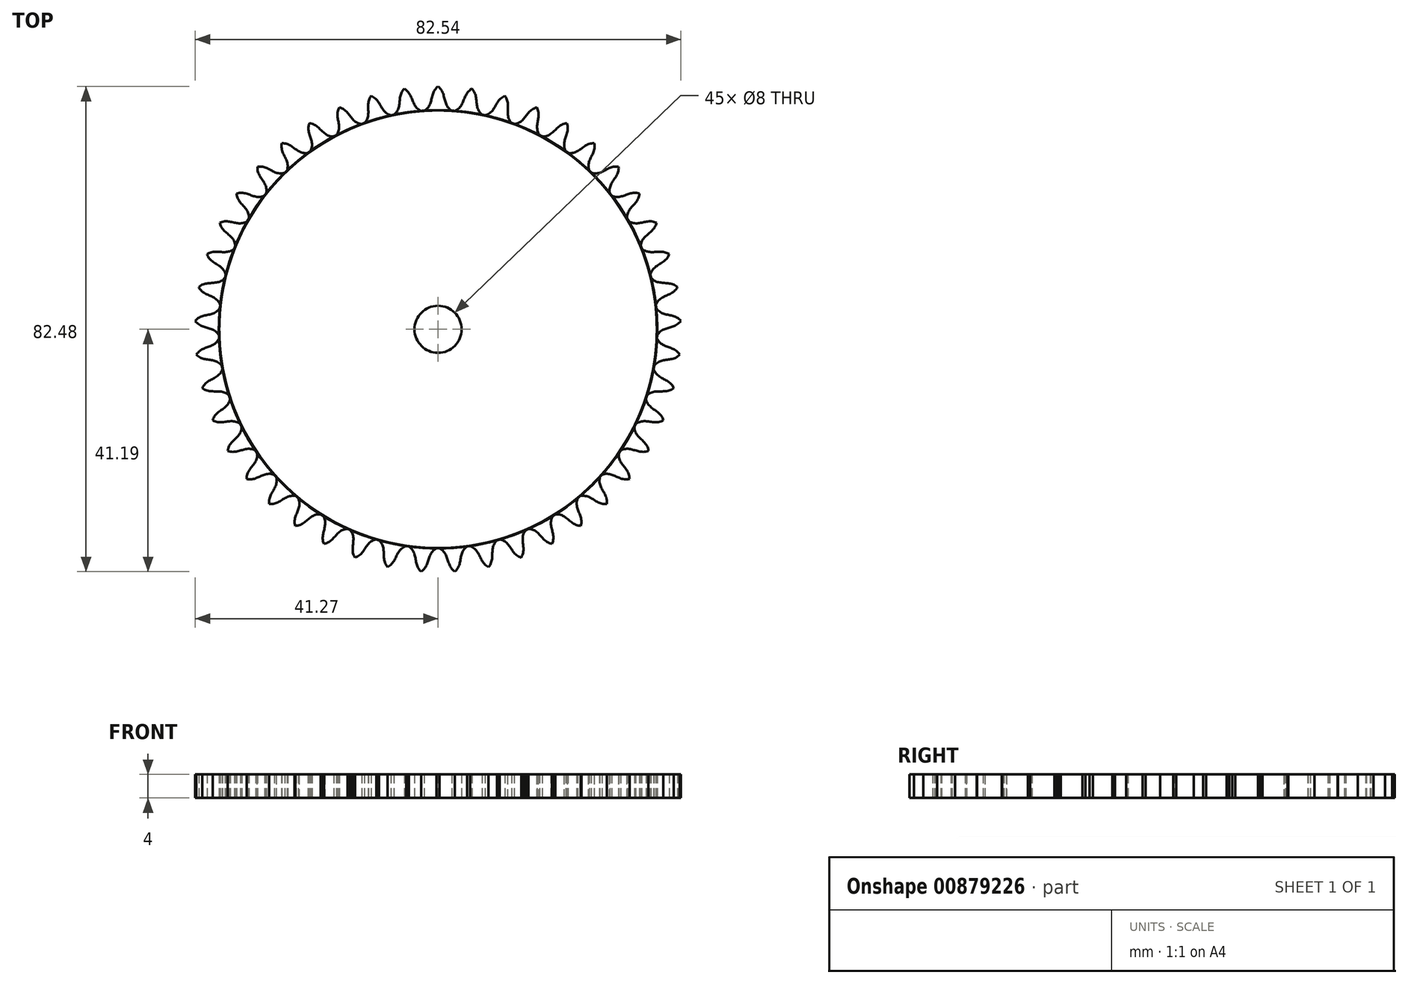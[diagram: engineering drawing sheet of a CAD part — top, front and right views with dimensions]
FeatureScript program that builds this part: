
annotation { "Feature Type Name" : "Feature", "Feature Type Description" : "" }
export const myFeature = defineFeature(function(context is Context, id is Id, definition is map)
    precondition{}
    {
        {
            assignVariable(context, id + "F0", {"name" : "GearWidth", "anyValue" : 4});
        }
        {
            assignVariable(context, id + "F1", {"name" : "TeethNumber", "anyValue" : 45});
        }
        {
            var Q0;
            Q0=qCreatedBy(makeId("Top.planeOp"),FACE);
            var sketch = newSketch(context, id + "F2", { "sketchPlane" : qUnion([Q0])});
            skLineSegment(sketch, "E0", {"start": v(0, 16.9) * mm, "end": v(0, -4.28) * mm, "construction": true});
            skCircle(sketch, "E1", {"center": v(0, 0) * mm, "radius": 37.24 * mm});
            skCircle(sketch, "E2", {"center": v(0, 0) * mm, "radius": 6 * mm});
            skCircle(sketch, "E3", {"center": v(0, 0) * mm, "radius": 4 * mm});
            skPoint(sketch, "E4", {"position": v(0, -6) * mm});
            skPoint(sketch, "E5", {"position": v(0, -5.14) * mm});
            skFitSpline(sketch, "E6", {"points": [v(0, 41.3) * mm, v(-2.35, 37.17) * mm], "startDerivative": vector(-4.5, -3.38) * mm, "endDerivative": vector(-5.1, -3) * mm});
            skFitSpline(sketch, "E7.MirrorCS", {"points": [v(0, 41.3) * mm, v(2.35, 37.17) * mm], "startDerivative": vector(4.5, -3.38) * mm, "endDerivative": vector(5.1, -3) * mm});
            skSolve(sketch);
        }
        {
            var Q0;
            Q0=makeQuery(id+"F2.imprint","IMPRINT",FACE,{"disambiguationData":[TD([[makeQuery(id+"F2.imprint","IMPRINT",EDGE,{"derivedFrom":sQuery(id+"F2.wireOp",EDGE,"E2")}),-1.0]])]});
            var Q1;
            Q1=makeQuery(id+"F2.imprint","IMPRINT",FACE,{"disambiguationData":[TD([[makeQuery(id+"F2.imprint","IMPRINT",EDGE,{"derivedFrom":sQuery(id+"F2.wireOp",EDGE,"E2")}),1.0]])]});
            var Q2;
            {var subQ0=sQuery(id+"F2.wireOp",EDGE,"E6");Q2=makeQuery(id+"F2.imprint","IMPRINT",FACE,{"disambiguationData":[TD([[makeQuery(id+"F2.imprint","IMPRINT",EDGE,{"derivedFrom":subQ0}),1.0]])]});}
            extrude(context, id + "F3", {"entities" : qUnion([Q0, Q1, Q2]), "depth" : (getVariable(context, 'GearWidth')) * mm, "offsetDistance" : 25 * mm});
        }
        {
            var Q0;
            Q0=makeQuery(id+"F3.opExtrude","SWEPT_BODY",BODY,{"disambiguationData":[OSD([sQuery(id+"F2.wireOp",EDGE,"f96d612a-3d40-4833-af0c-4c8240c050c0"),sQuery(id+"F2.wireOp",EDGE,"26c351bc-3793-4e67-ba11-eadc3bd423690.MirrorCS"),sQuery(id+"F2.wireOp",EDGE,"E1"),sQuery(id+"F2.wireOp",EDGE,"Xkr7LdUH-4pe8-4LZk-8Bcq-fOEmwItTBWrE")])]});
            var Q1;
            Q1=makeQuery(id+"F3.opExtrude","CAP_EDGE",EDGE,{"disambiguationData":[OSD([sQuery(id+"F2.wireOp",EDGE,"E3")])],"isStart":false});
            circularPattern(context, id + "F4", {"entities" : qUnion([Q0]), "axis" : qUnion([Q1]), "angle" : 360 * degree, "instanceCount" : getVariable(context, 'TeethNumber'), "equalSpace" : true});
        }
    });
